# Revit family: Rolling-Security-Grille_Cornell_SmokeShield_Fabric-Smoke-Fire_ERF20__1
name_source: partatom
category: Specialty Equipment
revit_build: Autodesk Revit 2018 (Build: 20170223_1515(x64)
units: mm (PartAtom-declared; Revit-internal decimal feet)

## family parameters
Always vertical = Yes
Cut with Voids When Loaded = No
OmniClass Number = 23.25.40.17.21
OmniClass Title = Coiling Partitions
Part Type = Normal
Room Calculation Point = No
Round Connector Dimension = Use Diameter
Shared = No
Work Plane-Based = Yes

## types (2) — shared parameters
Actual Height = 10' - 0"
Actual Width = 10' - 0"
Bottom Bar = Metal - Cornell - Steel RAL9010
Connector Description = Control box cable (Controller Can be Remotely Mounted)
Curtain = Newtex - Cornell - F920
Custom Size Warning = Size Available
Default Elevation = 0"
Description = Model ERF20

FIRE PROTECTION ALTERNATIVES FOR DESIGN VISIONARIES

LIMITLESS DESIGN FREEDON
We've take our nearly 100 years of experience in Smoke and Fire protection and annovated the SmokeShield Smoke and Fire. This curtain is an alternate method solution that allows the design visionary to pursue more unique layouts for atriums and other areas requiring compartmentalization.


PERFORMANCE WHILE MINIMIZING COSTS
SmokeShield Smoke and Fire's patented GuideLockTM technology positively seals the curtain within the guide channels, stopping smoke and fire migration in its tracks. Using this system can allow you to minimize or eliminate expensive smoke extraction systems, resulting in savings of weight, space and cost.

AESTHETICS
Design versatility allows guide surfaces to be easily concealed in wood, masonry, sheetrock or other fascia materials, offering the boadest range of mounting possibilities. Any exposed guides or bottom bars can be finished to match, complement, or contrast their surroundings with custom powder coat finishes. Finally, fasteners and shadow lines are invisible with our unique guide design.


SPACE
The headroom, backroom, and sideroom requirements are minimal and easily incorporated into your design.
Additionally the guide footprints for the SmokeShield Smoke and Fire are one of the smallest available.
Edition number = 1
Electrical Notes = For more information on the Electrical requirements please contact the manufacturer
Guides = Metal - Cornell - Steel RAL9010
Hood = Metal - Cornell - Steel RAL9010
Hood Depth = 10"
Hood Height = 11"
Manufacturer = Cornell
Model = ERF20
Number of Poles = 1
Opening Height = 10' - 0"
Opening Height MAX = 20' - 0"
Opening Height MIN = 6' - 0"
Opening Width = 10' - 0"
Opening Width MAX = 22' - 0"
Opening Width MIN = 4' - 0"
Phase = 1
Product Guid = 36292d1d-1939-4b07-8c08-6d6e85bfdb18
Product data url = https://www.bimobject.com
Sizing Disclaimer = Openings up to 57' wide and 20' high are standard construction. Consult Manufacturer for larger sizes
URL = https://www.cornelliron.com
Voltage = 115 V

## per-type parameters (varying)
| type | Assembly Height | Connector Angle | Distance Between Guides | Face of Wall | Power Factor | SideClearance | Tube Height |
| Face Of Wall | 10' - 11 1/2" | 90.00° | 10' - 0" | Yes | 1 | 6 3/4" | 10' - 0 3/8" |
| Between Jambs | 10' - 0" | 0.00° | 9' - 0" | No | 0 | 6" | 9' - 0 7/8" |

note: column(s) folded — value = type name in every type: Mounting

type visibility flags (boolean, named after types; folded from table):
- Face Of Wall: Yes: (none)
- Between Jambs: Yes: Between Jambs

## geometry (parser evidence)
native form markers: Sweep x5
no freeform markers — native parametric forms only
